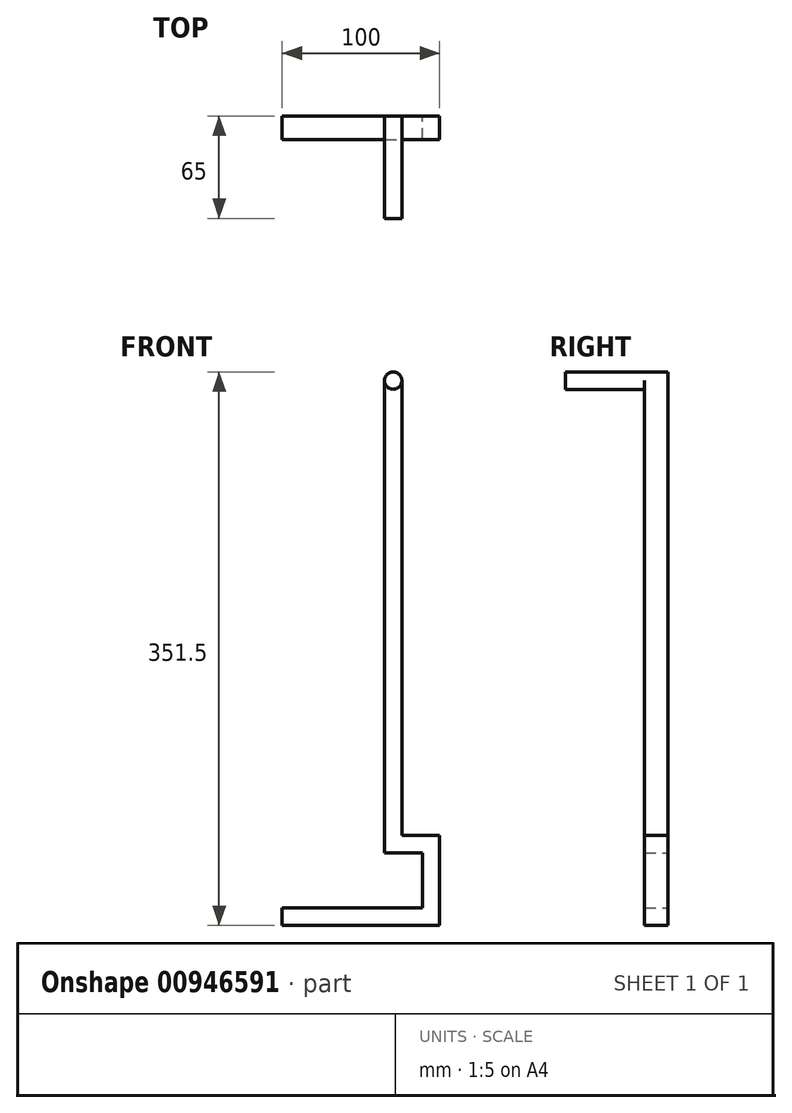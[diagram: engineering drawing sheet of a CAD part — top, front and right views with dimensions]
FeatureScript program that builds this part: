
annotation { "Feature Type Name" : "Feature", "Feature Type Description" : "" }
export const myFeature = defineFeature(function(context is Context, id is Id, definition is map)
    precondition{}
    {
        {
            var Q0;
            Q0=qCreatedBy(makeId("Front.planeOp"),FACE);
            var sketch = newSketch(context, id + "F0", { "sketchPlane" : qUnion([Q0])});
            skLineSegment(sketch, "E0", {"start": v(0, 311.23) * mm, "end": v(0, 22.23) * mm});
            skLineSegment(sketch, "E1", {"start": v(0, 22.23) * mm, "end": v(24, 22.23) * mm});
            skLineSegment(sketch, "E2", {"start": v(24, 22.23) * mm, "end": v(24, -34.77) * mm});
            skLineSegment(sketch, "E3", {"start": v(24, -34.77) * mm, "end": v(-76, -34.77) * mm});
            skLineSegment(sketch, "E4", {"start": v(-76, -34.77) * mm, "end": v(-76, -23.77) * mm});
            skLineSegment(sketch, "E5", {"start": v(-76, -23.77) * mm, "end": v(13, -23.77) * mm});
            skLineSegment(sketch, "E6", {"start": v(13, -23.77) * mm, "end": v(13, 11.23) * mm});
            skLineSegment(sketch, "E7", {"start": v(13, 11.23) * mm, "end": v(-11, 11.23) * mm});
            skLineSegment(sketch, "E8", {"start": v(-11, 11.23) * mm, "end": v(-11, 311.23) * mm});
            skArc(sketch, "E9", {"start": v(0, 311.23) * mm, "mid": v(-5.5, 316.73) * mm, "end": v(-11, 311.23) * mm});
            skSolve(sketch);
        }
        {
            var Q0;
            Q0 = qSketchRegion(id + "F0", true);
            extrude(context, id + "F1", {"entities" : qUnion([Q0]), "depth" : 15 * mm, "offsetDistance" : 25 * mm});
        }
        {
            var Q0;
            Q0=makeQuery(id+"F1.opExtrude","CAP_FACE",FACE,{"disambiguationData":[OSD([sQuery(id+"F0.wireOp",EDGE,"E0"),sQuery(id+"F0.wireOp",EDGE,"E1"),sQuery(id+"F0.wireOp",EDGE,"E2"),sQuery(id+"F0.wireOp",EDGE,"E3"),sQuery(id+"F0.wireOp",EDGE,"E4"),sQuery(id+"F0.wireOp",EDGE,"E5"),sQuery(id+"F0.wireOp",EDGE,"E6"),sQuery(id+"F0.wireOp",EDGE,"E7"),sQuery(id+"F0.wireOp",EDGE,"E8"),sQuery(id+"F0.wireOp",EDGE,"E9")])],"isStart":false});
            var sketch = newSketch(context, id + "F2", { "sketchPlane" : qUnion([Q0])});
            skCircle(sketch, "E10", {"center": v(-5.5, 311.23) * mm, "radius": 5.5 * mm});
            skSolve(sketch);
        }
        {
            var Q0;
            Q0 = qSketchRegion(id + "F2", true);
            extrude(context, id + "F3", {"entities" : qUnion([Q0]), "operationType" : NewBodyOperationType.ADD, "depth" : 50 * mm, "offsetDistance" : 25 * mm});
        }
    });
